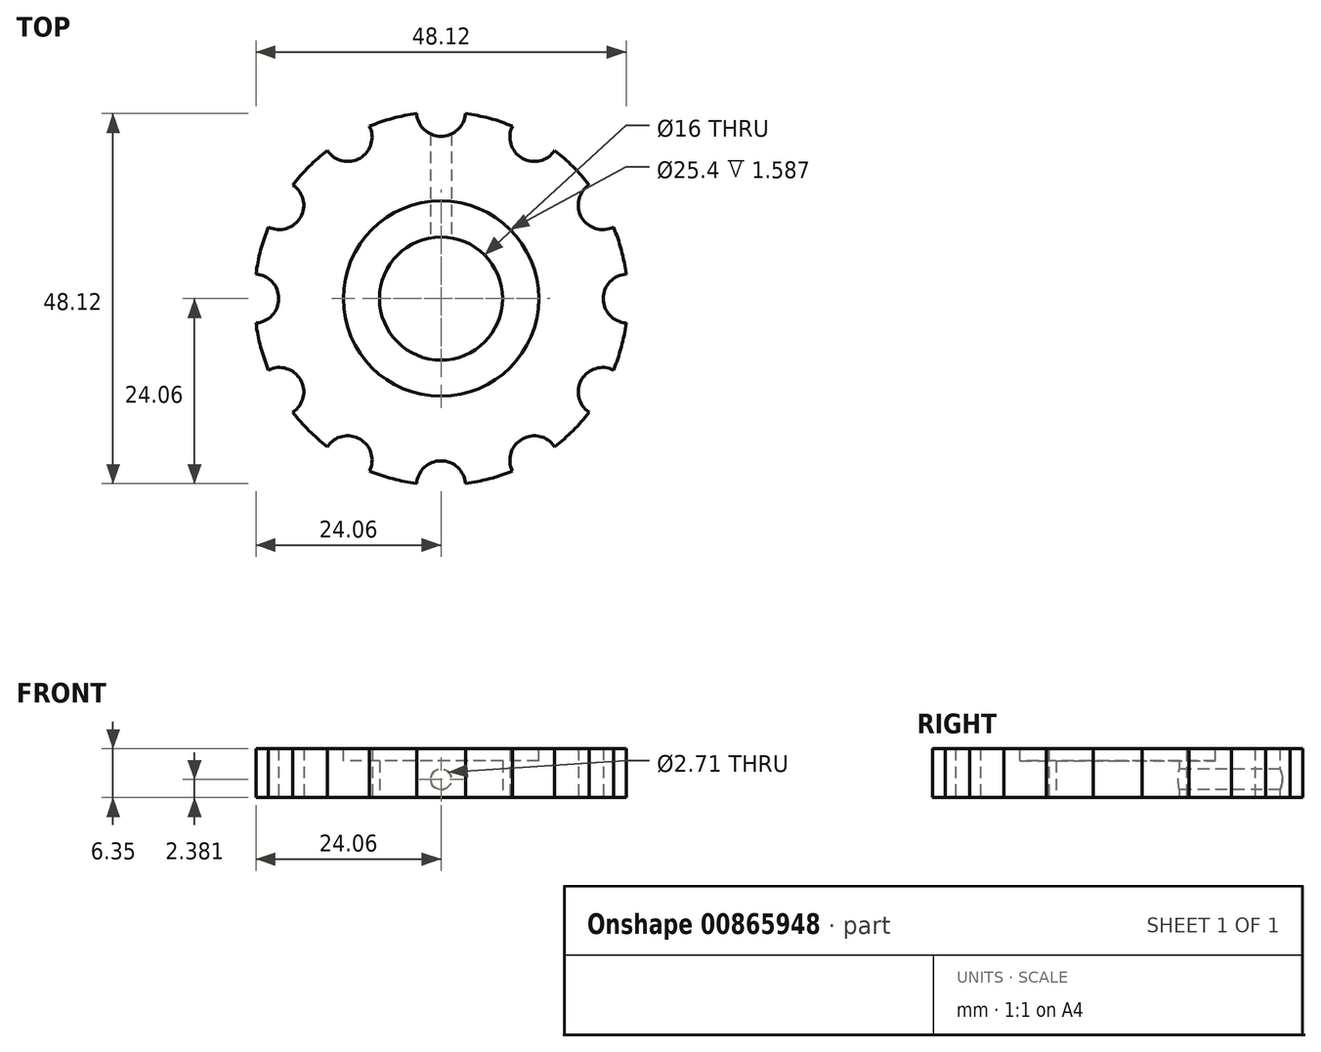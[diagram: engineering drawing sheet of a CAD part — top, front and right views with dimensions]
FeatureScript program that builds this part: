
annotation { "Feature Type Name" : "Feature", "Feature Type Description" : "" }
export const myFeature = defineFeature(function(context is Context, id is Id, definition is map)
    precondition{}
    {
        {
            var Q0;
            Q0=qCreatedBy(makeId("Top.planeOp"),FACE);
            var sketch = newSketch(context, id + "F0", { "sketchPlane" : qUnion([Q0])});
            skCircle(sketch, "E0", {"center": v(0, 0) * mm, "radius": 8 * mm});
            skArc(sketch, "E1", {"start": v(-3.17, 24.06) * mm, "mid": v(0, 21.1) * mm, "end": v(3.17, 24.06) * mm});
            skArc(sketch, "E2.1.0", {"start": v(-14.78, 19.26) * mm, "mid": v(-10.55, 18.27) * mm, "end": v(-9.29, 22.42) * mm});
            skArc(sketch, "E2.2.0", {"start": v(-22.42, 9.29) * mm, "mid": v(-18.27, 10.55) * mm, "end": v(-19.26, 14.78) * mm});
            skArc(sketch, "E2.3.0", {"start": v(-24.06, -3.17) * mm, "mid": v(-21.1, 0) * mm, "end": v(-24.06, 3.17) * mm});
            skArc(sketch, "E2.4.0", {"start": v(-19.26, -14.78) * mm, "mid": v(-18.27, -10.55) * mm, "end": v(-22.42, -9.29) * mm});
            skArc(sketch, "E2.5.0", {"start": v(-9.29, -22.42) * mm, "mid": v(-10.55, -18.27) * mm, "end": v(-14.78, -19.26) * mm});
            skArc(sketch, "E3.2.6.0", {"start": v(3.17, -24.06) * mm, "mid": v(0, -21.1) * mm, "end": v(-3.17, -24.06) * mm});
            skArc(sketch, "E3.2.7.0", {"start": v(14.78, -19.26) * mm, "mid": v(10.55, -18.27) * mm, "end": v(9.29, -22.42) * mm});
            skArc(sketch, "E3.2.8.0", {"start": v(22.42, -9.29) * mm, "mid": v(18.27, -10.55) * mm, "end": v(19.26, -14.78) * mm});
            skArc(sketch, "E3.2.9.0", {"start": v(24.06, 3.17) * mm, "mid": v(21.1, 0) * mm, "end": v(24.06, -3.17) * mm});
            skArc(sketch, "E3.2.10.0", {"start": v(19.26, 14.78) * mm, "mid": v(18.27, 10.55) * mm, "end": v(22.42, 9.29) * mm});
            skArc(sketch, "E3.2.11.0", {"start": v(9.29, 22.42) * mm, "mid": v(10.55, 18.27) * mm, "end": v(14.78, 19.26) * mm});
            skArc(sketch, "E4", {"start": v(-3.17, 24.06) * mm, "mid": v(-6.28, 23.45) * mm, "end": v(-9.29, 22.42) * mm});
            skArc(sketch, "E5.trimOffspring", {"start": v(9.29, 22.42) * mm, "mid": v(6.28, 23.45) * mm, "end": v(3.17, 24.06) * mm});
            skArc(sketch, "E6.trimOffspring", {"start": v(19.26, 14.78) * mm, "mid": v(17.16, 17.16) * mm, "end": v(14.78, 19.26) * mm});
            skArc(sketch, "E7.trimOffspring", {"start": v(24.06, 3.17) * mm, "mid": v(23.45, 6.28) * mm, "end": v(22.42, 9.29) * mm});
            skArc(sketch, "E8.trimOffspring", {"start": v(22.42, -9.29) * mm, "mid": v(23.45, -6.28) * mm, "end": v(24.06, -3.17) * mm});
            skArc(sketch, "E9.trimOffspring", {"start": v(14.78, -19.26) * mm, "mid": v(17.16, -17.16) * mm, "end": v(19.26, -14.78) * mm});
            skArc(sketch, "E10.trimOffspring", {"start": v(3.17, -24.06) * mm, "mid": v(6.28, -23.45) * mm, "end": v(9.29, -22.42) * mm});
            skArc(sketch, "E11.trimOffspring", {"start": v(-9.29, -22.42) * mm, "mid": v(-6.28, -23.45) * mm, "end": v(-3.17, -24.06) * mm});
            skArc(sketch, "E12.trimOffspring", {"start": v(-19.26, -14.78) * mm, "mid": v(-17.16, -17.16) * mm, "end": v(-14.78, -19.26) * mm});
            skArc(sketch, "E13.trimOffspring", {"start": v(-24.06, -3.17) * mm, "mid": v(-23.45, -6.28) * mm, "end": v(-22.42, -9.29) * mm});
            skArc(sketch, "E14.trimOffspring", {"start": v(-22.42, 9.29) * mm, "mid": v(-23.45, 6.28) * mm, "end": v(-24.06, 3.17) * mm});
            skArc(sketch, "E15.trimOffspring", {"start": v(-14.78, 19.26) * mm, "mid": v(-17.16, 17.16) * mm, "end": v(-19.26, 14.78) * mm});
            skLineSegment(sketch, "E16", {"start": v(-3.17, 24.06) * mm, "end": v(3.17, 24.06) * mm, "construction": true});
            skLineSegment(sketch, "E17", {"start": v(3.17, 24.06) * mm, "end": v(9.29, 22.42) * mm, "construction": true});
            skSolve(sketch);
        }
        {
            var Q0;
            Q0 = qSketchRegion(id + "F0", true);
            extrude(context, id + "F1", {"entities" : qUnion([Q0]), "depth" : 6.35 * mm, "offsetDistance" : 25.4 * mm});
        }
        {
            var Q0;
            Q0=makeQuery(id+"F1.opExtrude","CAP_FACE",FACE,{"disambiguationData":[OSD([sQuery(id+"F0.wireOp",EDGE,"E0"),sQuery(id+"F0.wireOp",EDGE,"E1"),sQuery(id+"F0.wireOp",EDGE,"E2.1.0"),sQuery(id+"F0.wireOp",EDGE,"E2.2.0"),sQuery(id+"F0.wireOp",EDGE,"E2.3.0"),sQuery(id+"F0.wireOp",EDGE,"E2.4.0"),sQuery(id+"F0.wireOp",EDGE,"E2.5.0"),sQuery(id+"F0.wireOp",EDGE,"E3.2.6.0"),sQuery(id+"F0.wireOp",EDGE,"E3.2.7.0"),sQuery(id+"F0.wireOp",EDGE,"E3.2.8.0"),sQuery(id+"F0.wireOp",EDGE,"E3.2.9.0"),sQuery(id+"F0.wireOp",EDGE,"E3.2.10.0"),sQuery(id+"F0.wireOp",EDGE,"E3.2.11.0"),sQuery(id+"F0.wireOp",EDGE,"E4"),sQuery(id+"F0.wireOp",EDGE,"E5.trimOffspring"),sQuery(id+"F0.wireOp",EDGE,"E6.trimOffspring"),sQuery(id+"F0.wireOp",EDGE,"E7.trimOffspring"),sQuery(id+"F0.wireOp",EDGE,"E8.trimOffspring"),sQuery(id+"F0.wireOp",EDGE,"E9.trimOffspring"),sQuery(id+"F0.wireOp",EDGE,"E10.trimOffspring"),sQuery(id+"F0.wireOp",EDGE,"E11.trimOffspring"),sQuery(id+"F0.wireOp",EDGE,"E12.trimOffspring"),sQuery(id+"F0.wireOp",EDGE,"E13.trimOffspring"),sQuery(id+"F0.wireOp",EDGE,"E14.trimOffspring"),sQuery(id+"F0.wireOp",EDGE,"E15.trimOffspring")])],"isStart":false});
            var sketch = newSketch(context, id + "F2", { "sketchPlane" : qUnion([Q0])});
            skCircle(sketch, "E18", {"center": v(0, 0) * mm, "radius": 12.7 * mm});
            skSolve(sketch);
        }
        {
            var Q0;
            Q0 = qSketchRegion(id + "F2", true);
            extrude(context, id + "F3", {"entities" : qUnion([Q0]), "operationType" : NewBodyOperationType.REMOVE, "oppositeDirection" : true, "depth" : 1.59 * mm, "offsetDistance" : 25.4 * mm});
        }
        {
            var Q0;
            Q0=qCreatedBy(makeId("Front.planeOp"),FACE);
            var Q1;
            Q1=makeQuery(id+"F1.opExtrude","CAP_VERTEX",VERTEX,{"disambiguationData":[OSD([sQuery(id+"F0.wireOp",EDGE,"E1"),sQuery(id+"F0.wireOp",EDGE,"E5.trimOffspring")])],"isStart":false});
            cPlane(context, id + "F4", {"entities" : qUnion([Q0, Q1]), "cplaneType" : CPlaneType.PLANE_POINT, "offset" : 25.4 * mm, "width" : 152.4 * mm, "height" : 152.4 * mm});
        }
        {
            var Q0;
            Q0=qCreatedBy(id+"F4.planeOp",FACE);
            var sketch = newSketch(context, id + "F5", { "sketchPlane" : qUnion([Q0])});
            skPoint(sketch, "E19", {"position": v(0, 2.38) * mm});
            skSolve(sketch);
        }
        {
            var Q0;
            Q0=sQuery(id+"F5.wireOp",VERTEX,"E19");
            var Q1;
            Q1=makeQuery(id+"F1.opExtrude","SWEPT_BODY",BODY,{"disambiguationData":[OSD([sQuery(id+"F0.wireOp",EDGE,"E0"),sQuery(id+"F0.wireOp",EDGE,"E1"),sQuery(id+"F0.wireOp",EDGE,"E2.1.0"),sQuery(id+"F0.wireOp",EDGE,"E2.2.0"),sQuery(id+"F0.wireOp",EDGE,"E2.3.0"),sQuery(id+"F0.wireOp",EDGE,"E2.4.0"),sQuery(id+"F0.wireOp",EDGE,"E2.5.0"),sQuery(id+"F0.wireOp",EDGE,"E3.2.6.0"),sQuery(id+"F0.wireOp",EDGE,"E3.2.7.0"),sQuery(id+"F0.wireOp",EDGE,"E3.2.8.0"),sQuery(id+"F0.wireOp",EDGE,"E3.2.9.0"),sQuery(id+"F0.wireOp",EDGE,"E3.2.10.0"),sQuery(id+"F0.wireOp",EDGE,"E3.2.11.0"),sQuery(id+"F0.wireOp",EDGE,"E4"),sQuery(id+"F0.wireOp",EDGE,"E5.trimOffspring"),sQuery(id+"F0.wireOp",EDGE,"E6.trimOffspring"),sQuery(id+"F0.wireOp",EDGE,"E7.trimOffspring"),sQuery(id+"F0.wireOp",EDGE,"E8.trimOffspring"),sQuery(id+"F0.wireOp",EDGE,"E9.trimOffspring"),sQuery(id+"F0.wireOp",EDGE,"E10.trimOffspring"),sQuery(id+"F0.wireOp",EDGE,"E11.trimOffspring"),sQuery(id+"F0.wireOp",EDGE,"E12.trimOffspring"),sQuery(id+"F0.wireOp",EDGE,"E13.trimOffspring"),sQuery(id+"F0.wireOp",EDGE,"E14.trimOffspring"),sQuery(id+"F0.wireOp",EDGE,"E15.trimOffspring")])]});
            hole(context, id + "F6", {"style" : HoleStyle.SIMPLE, "endStyle" : HoleEndStyle.BLIND, "oppositeDirection" : true, "standardTappedOrClearance" : lookupTablePath({ "standard" : "ANSI", "engagement" : "75%", "pitch" : "32 tpi", "size" : "#6", "type" : "Tapped" }), "standardBlindInLast" : lookupTablePath({ "standard" : "ANSI", "fit" : "Normal", "engagement" : "75%", "pitch" : "32 tpi", "size" : "#6", "type" : "Clearance & tapped" }), "holeDiameter" : 2.7 * mm, "majorDiameter" : 3.5 * mm, "showTappedDepth" : true, "holeDepth" : 19.05 * mm, "isTappedThrough" : true, "tappedDepth" : 16.67 * mm, "tapClearance" : 3, "locations" : qUnion([Q0]), "scope" : qUnion([Q1]), "startStyle" : HoleStartStyle.PART});
        }
    });
